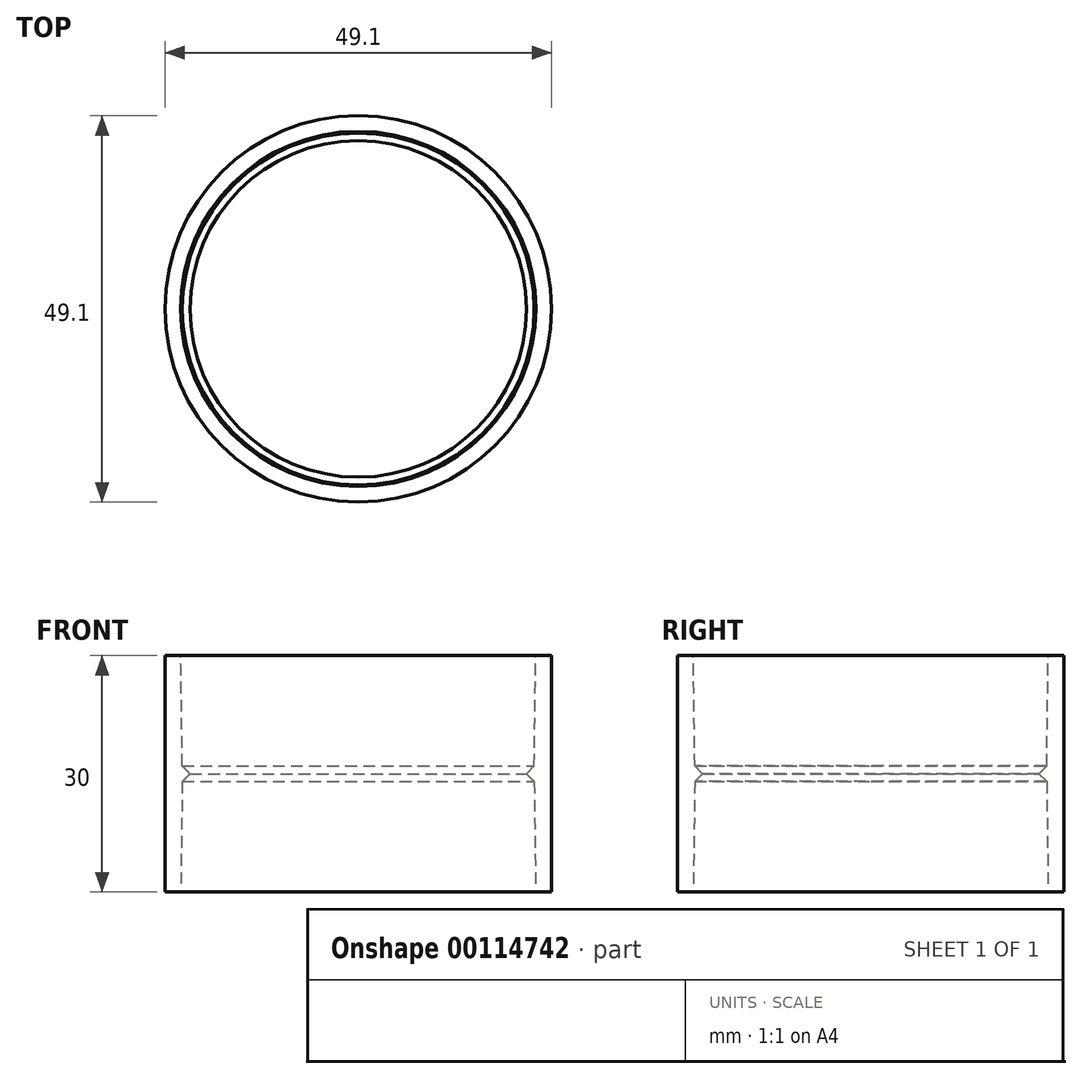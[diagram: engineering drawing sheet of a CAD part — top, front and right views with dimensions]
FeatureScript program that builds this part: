
annotation { "Feature Type Name" : "Feature", "Feature Type Description" : "" }
export const myFeature = defineFeature(function(context is Context, id is Id, definition is map)
    precondition{}
    {
        {
            var Q0;
            Q0=qCreatedBy(makeId("Front.planeOp"),FACE);
            var sketch = newSketch(context, id + "F0", { "sketchPlane" : qUnion([Q0])});
            skLineSegment(sketch, "E0", {"start": v(0, 0) * mm, "end": v(0, 30) * mm});
            skLineSegment(sketch, "E1", {"start": v(22.55, 0) * mm, "end": v(22.35, 14) * mm});
            skLineSegment(sketch, "E2", {"start": v(22.35, 16) * mm, "end": v(22.55, 30) * mm});
            skLineSegment(sketch, "E3", {"start": v(22.35, 14) * mm, "end": v(21.37, 15) * mm});
            skLineSegment(sketch, "E4", {"start": v(21.37, 15) * mm, "end": v(22.35, 16) * mm});
            skLineSegment(sketch, "E5", {"start": v(22.55, 30) * mm, "end": v(24.55, 30) * mm});
            skLineSegment(sketch, "E6", {"start": v(24.55, 30) * mm, "end": v(24.55, 0) * mm});
            skLineSegment(sketch, "E7", {"start": v(24.55, 0) * mm, "end": v(22.55, 0) * mm});
            skSolve(sketch);
        }
        {
            var Q0;
            Q0=makeQuery(id+"F0.imprint","IMPRINT",FACE,{"disambiguationData":[TD([[makeQuery(id+"F0.imprint","IMPRINT",EDGE,{"derivedFrom":sQuery(id+"F0.wireOp",EDGE,"E1")}),-1.0]])]});
            var Q1;
            Q1=sQuery(id+"F0.wireOp",EDGE,"E0");
            revolve(context, id + "F1", {"entities" : qUnion([Q0]), "axis" : qUnion([Q1]), "revolveType" : RevolveType.FULL});
        }
    });
